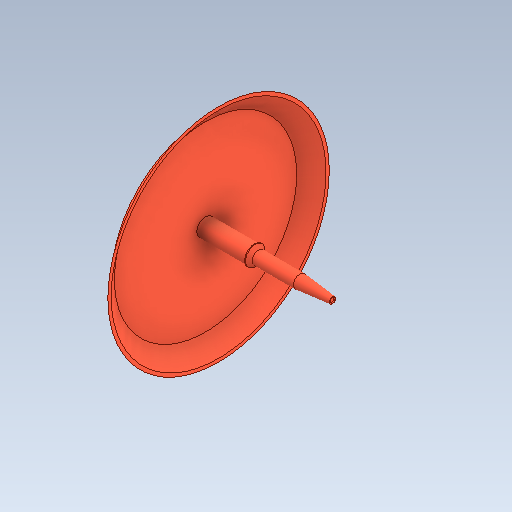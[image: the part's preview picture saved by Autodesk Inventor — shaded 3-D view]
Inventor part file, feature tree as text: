
AUTODESK INVENTOR PART (.ipt)
format: ipt  version: 2020 (Build 240168000, 168)  size: 207,360 bytes
history: native  units: mm
features: sketch x11, extrude x8, fillet x3, revolve x2, plane x1, chamfer x1
ambient origin geometry x8: Origin, YZ Plane, XZ Plane, XY Plane, X Axis, Y Axis, Z Axis, Center Point
bodies: Solid1 (feature_tree)
feature tree (26):
  extrude  "Extrusion1"  Depth=28.0mm
  plane  "Work Plane1"
  sketch  "Sketch2"  dims[d2=0.4mm d3=0.0mm d4=2.0mm]
  revolve  "Revolution1"  [1 undecoded]
  extrude  "Extrusion2"  TaperAngle=90.0deg  [1 undecoded]
  fillet  "Fillet1"  Radius=9.0mm
  extrude  "Extrusion3"  Depth=2.0mm
  extrude  "Extrusion4"  Depth=3.0mm TaperAngle=0.0deg
  extrude  "Extrusion5"  Depth=7.5mm TaperAngle=0.0deg
  extrude  "Extrusion6"  Depth=3.0mm TaperAngle=0.0deg
  chamfer  "Chamfer1"  Distance=11.86mm
  revolve  "Revolution2"  [1 undecoded]
  extrude  "Extrusion7"  TaperAngle=90.0deg  [1 undecoded]
  fillet  "Fillet2"  Radius=0.8mm
  extrude  "Extrusion8"  Depth=0.1mm
  fillet  "Fillet3"  Radius=6.5mm
  sketch  "Sketch1"  dims[d0=34.0mm d1=28.0mm]
  sketch  "Sketch3"  dims[d5=34.0mm d6=90.0deg d7=9.0mm]
  sketch  "Sketch4"  dims[d8=0.6mm d9=0.0mm d10=2.0mm]
  sketch  "Sketch5"  dims[d11=2.0mm d12=3.0mm d13=0.0mm]
  sketch  "Sketch6"  dims[d14=2.7mm d15=7.5mm d16=0.0mm]
  sketch  "Sketch7"  dims[d17=3.0mm d18=0.14mm d19=0.0mm]
  sketch  "Sketch8"  dims[d20=2.0mm d21=11.86mm d22=0.0mm]
  sketch  "Sketch9"  dims[d23=0.5mm d24=2.0mm d25=45.0deg d26=0.5mm]
  sketch  "Sketch10"  dims[d27=5.0mm d28=90.0deg d29=0.8mm]
  sketch  "Sketch11"  dims[d30=0.1mm d31=0.0mm d32=0.1mm d33=6.5mm d34=0.1mm d35=0.0mm d36=0.1mm]
note: 4 required parameter values undecoded (feature->parameter linkage not recoverable at this tier; creation-order binding heuristic only, values carry confidence <= 0.55)